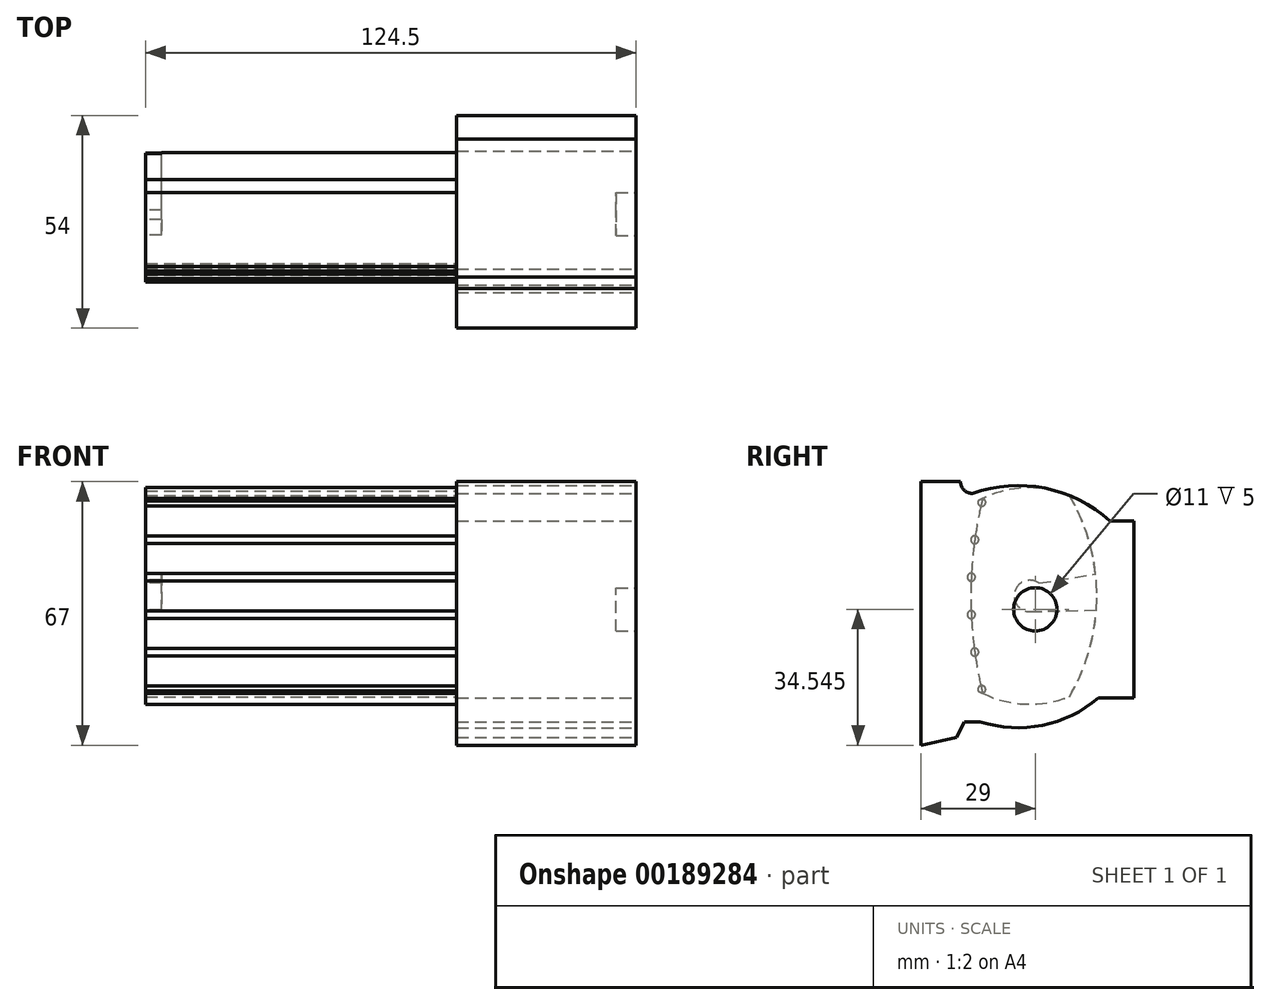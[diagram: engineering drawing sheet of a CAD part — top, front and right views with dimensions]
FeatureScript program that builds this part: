
annotation { "Feature Type Name" : "Feature", "Feature Type Description" : "" }
export const myFeature = defineFeature(function(context is Context, id is Id, definition is map)
    precondition{}
    {
        {
            var Q0;
            Q0=qCreatedBy(makeId("Right.planeOp"),FACE);
            var sketch = newSketch(context, id + "F0", { "sketchPlane" : qUnion([Q0])});
            skLineSegment(sketch, "E0", {"start": v(0, 0) * mm, "end": v(0, 45) * mm});
            skLineSegment(sketch, "E1", {"start": v(0, 45) * mm, "end": v(-6, 45) * mm});
            skLineSegment(sketch, "E2", {"start": v(0, 0) * mm, "end": v(-9, 0) * mm});
            skArc(sketch, "E3", {"start": v(-6, 45) * mm, "mid": v(-22.53, 53.33) * mm, "end": v(-41, 52) * mm});
            skLineSegment(sketch, "E4", {"start": v(-6, 45) * mm, "end": v(-41, 45) * mm, "construction": true});
            skLineSegment(sketch, "E5", {"start": v(-41, 45) * mm, "end": v(-41, 52) * mm, "construction": true});
            skLineSegment(sketch, "E6", {"start": v(-9, 0) * mm, "end": v(-39, 0) * mm, "construction": true});
            skLineSegment(sketch, "E7", {"start": v(-39, 0) * mm, "end": v(-39, -6) * mm, "construction": true});
            skArc(sketch, "E8", {"start": v(-39, -6) * mm, "mid": v(-23.22, -6.92) * mm, "end": v(-9, 0) * mm});
            skLineSegment(sketch, "E9", {"start": v(-29.35, 45) * mm, "end": v(-29.35, 0) * mm, "construction": true});
            skLineSegment(sketch, "E10", {"start": v(0, 20.42) * mm, "end": v(-29.35, 20.42) * mm, "construction": true});
            skLineSegment(sketch, "E11", {"start": v(-39, -6) * mm, "end": v(-43, -6) * mm});
            skLineSegment(sketch, "E12", {"start": v(-41, 52) * mm, "end": v(-41, 52) * mm});
            skLineSegment(sketch, "E13", {"start": v(-44, 55) * mm, "end": v(-44, 55) * mm});
            skPoint(sketch, "E14.visualSharp", {"position": v(-44, 52) * mm});
            skArc(sketch, "E14.filletArc", {"start": v(-44, 55) * mm, "mid": v(-43.12, 52.88) * mm, "end": v(-41, 52) * mm});
            skLineSegment(sketch, "E15", {"start": v(-43, -6) * mm, "end": v(-45, -6) * mm, "construction": true});
            skLineSegment(sketch, "E16", {"start": v(-45, -10) * mm, "end": v(-45, -6) * mm, "construction": true});
            skLineSegment(sketch, "E17", {"start": v(-43, -6) * mm, "end": v(-45, -10) * mm});
            skLineSegment(sketch, "E18", {"start": v(-44, 55) * mm, "end": v(-54, 55) * mm});
            skLineSegment(sketch, "E19", {"start": v(-54, 55) * mm, "end": v(-54, -12) * mm});
            skLineSegment(sketch, "E20", {"start": v(-54, -12) * mm, "end": v(-45, -10) * mm});
            skLineSegment(sketch, "E21", {"start": v(-25, 22.5) * mm, "end": v(0, 22.5) * mm, "construction": true});
            skLineSegment(sketch, "E22", {"start": v(-25, 45) * mm, "end": v(-25, 0) * mm, "construction": true});
            skPoint(sketch, "E22.startSnap0", {"position": v(-23.5, 45) * mm});
            skSolve(sketch);
        }
        {
            var Q0;
            Q0=makeQuery(id+"F0.imprint","IMPRINT",FACE,{"disambiguationData":[TD([[makeQuery(id+"F0.imprint","IMPRINT",EDGE,{"derivedFrom":sQuery(id+"F0.wireOp",EDGE,"E0")}),1.0]])]});
            extrude(context, id + "F1", {"entities" : qUnion([Q0]), "oppositeDirection" : true, "depth" : 45.5 * mm});
        }
        {
            var Q0;
            Q0=makeQuery(id+"F0.imprint","IMPRINT",FACE,{"disambiguationData":[TD([[makeQuery(id+"F0.imprint","IMPRINT",EDGE,{"derivedFrom":sQuery(id+"F0.wireOp",EDGE,"E0")}),1.0]])]});
            var sketch = newSketch(context, id + "F2", { "sketchPlane" : qUnion([Q0])});
            skCircle(sketch, "E23", {"center": v(-25, 22.54) * mm, "radius": 5.5 * mm});
            skSolve(sketch);
        }
        {
            var Q0;
            Q0=makeQuery(id+"F2.imprint","IMPRINT",FACE,{"disambiguationData":[TD([[makeQuery(id+"F2.imprint","IMPRINT",EDGE,{"derivedFrom":sQuery(id+"F2.wireOp",EDGE,"E23")}),1.0]])]});
            var Q1;
            Q1=sQuery(id+"F2.wireOp",EDGE,"E23");
            extrude(context, id + "F3", {"entities" : qUnion([Q0]), "operationType" : NewBodyOperationType.REMOVE, "surfaceEntities" : qUnion([Q1]), "oppositeDirection" : true, "depth" : 5 * mm});
        }
        {
            var Q0;
            Q0=makeQuery(id+"F1.opExtrude","CAP_FACE",FACE,{"disambiguationData":[OSD([sQuery(id+"F0.wireOp",EDGE,"E0"),sQuery(id+"F0.wireOp",EDGE,"E1"),sQuery(id+"F0.wireOp",EDGE,"E2"),sQuery(id+"F0.wireOp",EDGE,"E3"),sQuery(id+"F0.wireOp",EDGE,"E8"),sQuery(id+"F0.wireOp",EDGE,"E11"),sQuery(id+"F0.wireOp",EDGE,"E14.filletArc"),sQuery(id+"F0.wireOp",EDGE,"E17"),sQuery(id+"F0.wireOp",EDGE,"E18"),sQuery(id+"F0.wireOp",EDGE,"E19"),sQuery(id+"F0.wireOp",EDGE,"E20")])],"isStart":false});
            var sketch = newSketch(context, id + "F4", { "sketchPlane" : qUnion([Q0])});
            skCircle(sketch, "E24", {"center": v(26.36, 25.95) * mm, "radius": 27.5 * mm});
            skLineSegment(sketch, "E25", {"start": v(26.36, 25.95) * mm, "end": v(41.36, 25.95) * mm, "construction": true});
            skLineSegment(sketch, "E26", {"start": v(26.36, 25.95) * mm, "end": v(9.36, 25.95) * mm, "construction": true});
            skLineSegment(sketch, "E27", {"start": v(26.36, 53.45) * mm, "end": v(26.36, -1.55) * mm, "construction": true});
            skLineSegment(sketch, "E28", {"start": v(26.36, 51.57) * mm, "end": v(16.36, 51.57) * mm, "construction": true});
            skLineSegment(sketch, "E29", {"start": v(26.36, 50.7) * mm, "end": v(38.36, 50.7) * mm, "construction": true});
            skLineSegment(sketch, "E30", {"start": v(26.36, 1.21) * mm, "end": v(38.36, 1.21) * mm, "construction": true});
            skLineSegment(sketch, "E31", {"start": v(26.36, 0.34) * mm, "end": v(16.36, 0.34) * mm, "construction": true});
            skArc(sketch, "E32", {"start": v(38.36, 1.21) * mm, "mid": v(41.36, 25.95) * mm, "end": v(38.36, 50.7) * mm});
            skArc(sketch, "E33", {"start": v(16.36, 51.57) * mm, "mid": v(9.36, 25.95) * mm, "end": v(16.36, 0.34) * mm});
            skCircle(sketch, "E34", {"center": v(38.6, 49.74) * mm, "radius": 1 * mm});
            skCircle(sketch, "E35", {"center": v(38.6, 2.18) * mm, "radius": 1 * mm});
            skCircle(sketch, "E36", {"center": v(40.37, 40.23) * mm, "radius": 1 * mm});
            skCircle(sketch, "E37", {"center": v(40.37, 11.69) * mm, "radius": 1 * mm});
            skCircle(sketch, "E38", {"center": v(41.25, 21.2) * mm, "radius": 1 * mm});
            skCircle(sketch, "E39", {"center": v(41.25, 30.72) * mm, "radius": 1 * mm});
            skSolve(sketch);
        }
        {
            var Q0;
            {var subQ0=sQuery(id+"F4.wireOp",EDGE,"E24");var subQ4=makeQuery(id+"F1.opExtrude","CAP_EDGE",EDGE,{"disambiguationData":[OSD([sQuery(id+"F0.wireOp",EDGE,"E3")])],"isStart":false});var subQ8=makeQuery(id+"F4.imprint","INTERSECT",VERTEX,{"disambiguationData":[OD(0.0)],"derivedFrom":[subQ4,subQ0]});Q0=makeQuery(id+"F4.imprint","IMPRINT",FACE,{"disambiguationData":[TD([[makeQuery(id+"F4.imprint","IMPRINT",EDGE,{"disambiguationData":[TD([[subQ8,1.0]])],"derivedFrom":subQ0}),1.0]])]});}
            var Q1;
            {var subQ0=sQuery(id+"F4.wireOp",EDGE,"E32");var subQ1=sQuery(id+"F4.wireOp",EDGE,"E24");var subQ2=makeQuery(id+"F4.imprint","INTERSECT",VERTEX,{"disambiguationData":[OD(1.0)],"derivedFrom":[subQ1,subQ0]});Q1=makeQuery(id+"F4.imprint","IMPRINT",FACE,{"disambiguationData":[TD([[makeQuery(id+"F4.imprint","IMPRINT",EDGE,{"disambiguationData":[TD([[subQ2,1.0]])],"derivedFrom":subQ1}),1.0]])]});}
            var Q2;
            {var subQ0=sQuery(id+"F4.wireOp",EDGE,"E39");var subQ1=sQuery(id+"F4.wireOp",EDGE,"E32");var subQ2=makeQuery(id+"F4.imprint","INTERSECT",VERTEX,{"disambiguationData":[OD(0.0)],"derivedFrom":[subQ1,subQ0]});Q2=makeQuery(id+"F4.imprint","IMPRINT",FACE,{"disambiguationData":[TD([[makeQuery(id+"F4.imprint","IMPRINT",EDGE,{"disambiguationData":[TD([[subQ2,-1.0]])],"derivedFrom":subQ1}),-1.0]])]});}
            var Q3;
            {var subQ0=sQuery(id+"F4.wireOp",EDGE,"E38");var subQ1=sQuery(id+"F4.wireOp",EDGE,"E32");var subQ2=makeQuery(id+"F4.imprint","INTERSECT",VERTEX,{"disambiguationData":[OD(0.0)],"derivedFrom":[subQ1,subQ0]});Q3=makeQuery(id+"F4.imprint","IMPRINT",FACE,{"disambiguationData":[TD([[makeQuery(id+"F4.imprint","IMPRINT",EDGE,{"disambiguationData":[TD([[subQ2,-1.0]])],"derivedFrom":subQ1}),-1.0]])]});}
            var Q4;
            {var subQ0=sQuery(id+"F4.wireOp",EDGE,"E37");var subQ1=sQuery(id+"F4.wireOp",EDGE,"E32");var subQ2=makeQuery(id+"F4.imprint","INTERSECT",VERTEX,{"disambiguationData":[OD(0.0)],"derivedFrom":[subQ1,subQ0]});Q4=makeQuery(id+"F4.imprint","IMPRINT",FACE,{"disambiguationData":[TD([[makeQuery(id+"F4.imprint","IMPRINT",EDGE,{"disambiguationData":[TD([[subQ2,-1.0]])],"derivedFrom":subQ1}),-1.0]])]});}
            var Q5;
            {var subQ0=sQuery(id+"F4.wireOp",EDGE,"E32");var subQ1=sQuery(id+"F4.wireOp",EDGE,"E24");var subQ2=makeQuery(id+"F4.imprint","INTERSECT",VERTEX,{"disambiguationData":[OD(0.0)],"derivedFrom":[subQ1,subQ0]});Q5=makeQuery(id+"F4.imprint","IMPRINT",FACE,{"disambiguationData":[TD([[makeQuery(id+"F4.imprint","IMPRINT",EDGE,{"disambiguationData":[TD([[subQ2,-1.0]])],"derivedFrom":subQ1}),1.0]])]});}
            var Q6;
            {var subQ0=sQuery(id+"F4.wireOp",EDGE,"E36");var subQ1=sQuery(id+"F4.wireOp",EDGE,"E32");var subQ2=makeQuery(id+"F4.imprint","INTERSECT",VERTEX,{"disambiguationData":[OD(0.0)],"derivedFrom":[subQ1,subQ0]});Q6=makeQuery(id+"F4.imprint","IMPRINT",FACE,{"disambiguationData":[TD([[makeQuery(id+"F4.imprint","IMPRINT",EDGE,{"disambiguationData":[TD([[subQ2,-1.0]])],"derivedFrom":subQ1}),-1.0]])]});}
            extrude(context, id + "F5", {"entities" : qUnion([Q0, Q1, Q2, Q3, Q4, Q5, Q6]), "depth" : 79 * mm});
        }
        {
            var Q0;
            Q0=makeQuery(id+"F5.opExtrude","CAP_FACE",FACE,{"disambiguationData":[OSD([sQuery(id+"F0.wireOp",EDGE,"E3"),sQuery(id+"F4.wireOp",EDGE,"E24"),sQuery(id+"F4.wireOp",EDGE,"E32"),sQuery(id+"F4.wireOp",EDGE,"E33")])],"isStart":false});
            var sketch = newSketch(context, id + "F6", { "sketchPlane" : qUnion([Q0])});
            skCircle(sketch, "E40", {"center": v(26.36, 25.95) * mm, "radius": 4 * mm});
            skLineSegment(sketch, "E41", {"start": v(24.04, 29.21) * mm, "end": v(9.67, 31.56) * mm});
            skLineSegment(sketch, "E42", {"start": v(26.36, 21.95) * mm, "end": v(9.49, 22.4) * mm});
            skSolve(sketch);
        }
        {
            var Q0;
            {var subQ0=sQuery(id+"F6.wireOp",EDGE,"E41");Q0=makeQuery(id+"F6.imprint","IMPRINT",FACE,{"disambiguationData":[TD([[makeQuery(id+"F6.imprint","IMPRINT",EDGE,{"derivedFrom":subQ0}),1.0]])]});}
            var Q1;
            {var subQ0=sQuery(id+"F6.wireOp",EDGE,"E40");var subQ1=makeQuery(id+"F6.imprint","INTERSECT",VERTEX,{"derivedFrom":[subQ0,sQuery(id+"F6.wireOp",EDGE,"E41")]});Q1=makeQuery(id+"F6.imprint","IMPRINT",FACE,{"disambiguationData":[TD([[makeQuery(id+"F6.imprint","IMPRINT",EDGE,{"disambiguationData":[TD([[subQ1,-1.0]])],"derivedFrom":subQ0}),1.0]])]});}
            extrude(context, id + "F7", {"entities" : qUnion([Q0, Q1]), "operationType" : NewBodyOperationType.REMOVE, "oppositeDirection" : true, "depth" : 4 * mm});
        }
    });
